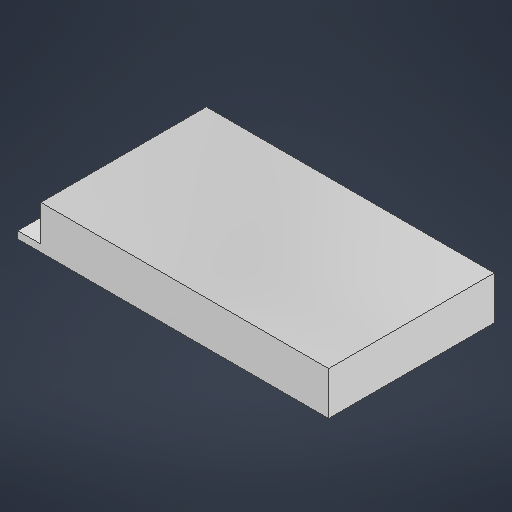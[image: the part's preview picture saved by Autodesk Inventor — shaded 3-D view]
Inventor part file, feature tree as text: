
AUTODESK INVENTOR PART (.ipt)
format: ipt  version: 2025.1 (Build 291241000, 241)  size: 194,560 bytes
history: native  units: mm
features: extrude x3, sketch x3, projected_geometry x2
ambient origin geometry x8: Origin, YZ Plane, XZ Plane, XY Plane, X Axis, Y Axis, Z Axis, Center Point
bodies: Solid1 (feature_tree)
feature tree (8):
  extrude  "Extrusion1"  Depth=115.0mm
  extrude  "Extrusion2"  Depth=16.0mm
  extrude  "Extrusion3"  Depth=4.0mm
  sketch  "Sketch1"  dims[d0=215.9mm d1=115.0mm]
  sketch  "Sketch2"  dims[d2=30.0mm d3=0.0mm d4=16.0mm]
  projected_geometry  "Projected Loop1"
  sketch  "Sketch3"  dims[d5=25.0mm d6=0.0mm d7=150.0mm d8=50.0mm d9=32.0mm d10=4.0mm d11=4.0mm d12=0.0mm]
  projected_geometry  "Projected Loop2"
